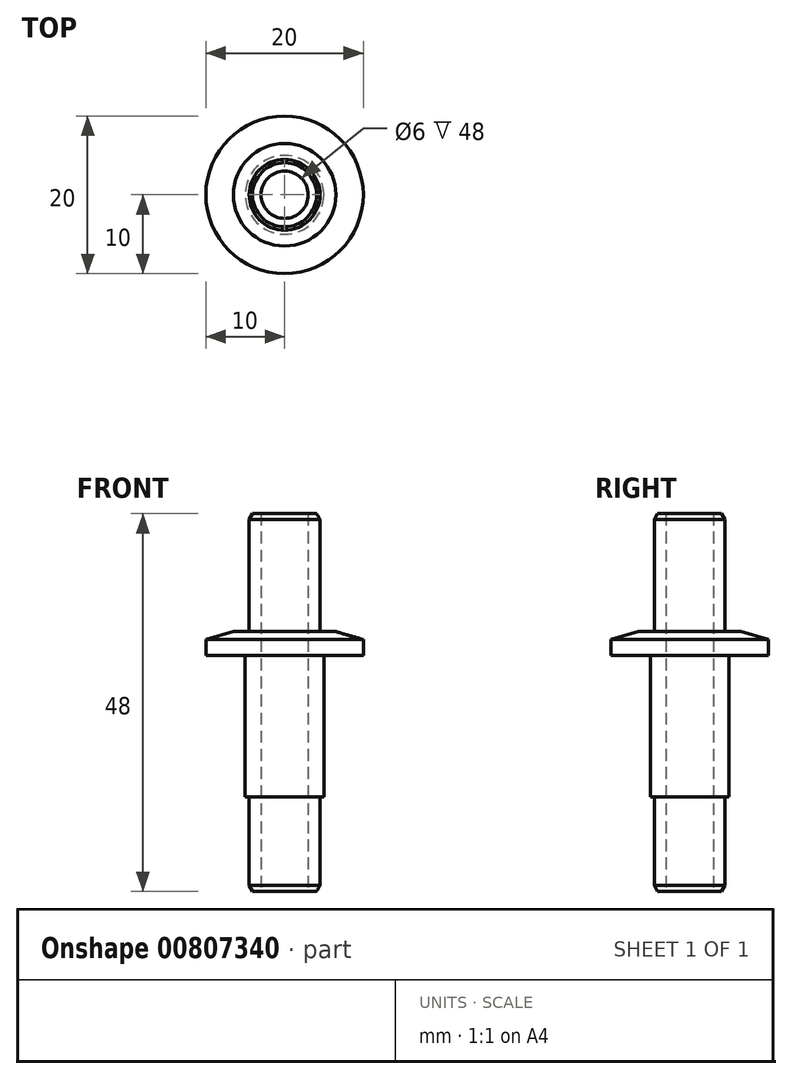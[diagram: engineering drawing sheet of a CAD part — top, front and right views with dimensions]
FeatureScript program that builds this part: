
annotation { "Feature Type Name" : "Feature", "Feature Type Description" : "" }
export const myFeature = defineFeature(function(context is Context, id is Id, definition is map)
    precondition{}
    {
        {
            var Q0;
            Q0=qCreatedBy(makeId("Top.planeOp"),FACE);
            var sketch = newSketch(context, id + "F0", { "sketchPlane" : qUnion([Q0])});
            skCircle(sketch, "E0", {"center": v(0, 0) * mm, "radius": 4.5 * mm});
            skSolve(sketch);
        }
        {
            var Q0;
            Q0 = qSketchRegion(id + "F0", true);
            extrude(context, id + "F1", {"entities" : qUnion([Q0]), "depth" : 12 * mm, "offsetDistance" : 25 * mm});
        }
        {
            var Q0;
            Q0=makeQuery(id+"F1.opExtrude","CAP_FACE",FACE,{"disambiguationData":[OSD([sQuery(id+"F0.wireOp",EDGE,"E0")])],"isStart":false});
            var sketch = newSketch(context, id + "F2", { "sketchPlane" : qUnion([Q0])});
            skCircle(sketch, "E1", {"center": v(0, 0) * mm, "radius": 5 * mm});
            skSolve(sketch);
        }
        {
            var Q0;
            Q0 = qSketchRegion(id + "F2", true);
            extrude(context, id + "F3", {"entities" : qUnion([Q0]), "operationType" : NewBodyOperationType.ADD, "depth" : 18 * mm, "offsetDistance" : 25 * mm});
        }
        {
            var Q0;
            Q0=makeQuery(id+"F3.opExtrude","CAP_FACE",FACE,{"disambiguationData":[OSD([sQuery(id+"F2.wireOp",EDGE,"E1")])],"isStart":false});
            var sketch = newSketch(context, id + "F4", { "sketchPlane" : qUnion([Q0])});
            skCircle(sketch, "E2", {"center": v(0, 0) * mm, "radius": 10 * mm});
            skSolve(sketch);
        }
        {
            var Q0;
            Q0 = qSketchRegion(id + "F4", true);
            extrude(context, id + "F5", {"entities" : qUnion([Q0]), "operationType" : NewBodyOperationType.ADD, "depth" : 3 * mm, "offsetDistance" : 25 * mm});
        }
        {
            var Q0;
            Q0=makeQuery(id+"F5.opExtrude","CAP_FACE",FACE,{"disambiguationData":[OSD([sQuery(id+"F4.wireOp",EDGE,"E2")])],"isStart":false});
            var sketch = newSketch(context, id + "F6", { "sketchPlane" : qUnion([Q0])});
            skCircle(sketch, "E3", {"center": v(0, 0) * mm, "radius": 4.5 * mm});
            skSolve(sketch);
        }
        {
            var Q0;
            Q0 = qSketchRegion(id + "F6", true);
            extrude(context, id + "F7", {"entities" : qUnion([Q0]), "operationType" : NewBodyOperationType.ADD, "depth" : 15 * mm, "offsetDistance" : 25 * mm});
        }
        {
            var Q0;
            Q0=makeQuery(id+"F1.opExtrude","CAP_FACE",FACE,{"disambiguationData":[OSD([sQuery(id+"F0.wireOp",EDGE,"E0")])],"isStart":true});
            var sketch = newSketch(context, id + "F8", { "sketchPlane" : qUnion([Q0])});
            skCircle(sketch, "E4", {"center": v(0, 0) * mm, "radius": 3 * mm});
            skSolve(sketch);
        }
        {
            var Q0;
            Q0 = qSketchRegion(id + "F8", true);
            extrude(context, id + "F9", {"entities" : qUnion([Q0]), "operationType" : NewBodyOperationType.REMOVE, "endBound" : BoundingType.THROUGH_ALL, "oppositeDirection" : true, "depth" : 25 * mm, "offsetDistance" : 25 * mm});
        }
        {
            var Q0;
            Q0=makeQuery(id+"F7.opExtrude","CAP_EDGE",EDGE,{"disambiguationData":[OSD([sQuery(id+"F6.wireOp",EDGE,"E3")])],"isStart":false});
            chamfer(context, id + "F10", {"entities" : qUnion([Q0]), "chamferType" : ChamferType.OFFSET_ANGLE, "width" : 0.75 * mm, "oppositeDirection" : true, "angle" : 30 * degree});
        }
        {
            var Q0;
            Q0=makeQuery(id+"F1.opExtrude","CAP_EDGE",EDGE,{"disambiguationData":[OSD([sQuery(id+"F0.wireOp",EDGE,"E0")])],"isStart":true});
            chamfer(context, id + "F11", {"entities" : qUnion([Q0]), "chamferType" : ChamferType.OFFSET_ANGLE, "width" : 0.75 * mm, "oppositeDirection" : false, "angle" : 30 * degree, "tangentPropagation" : true});
        }
        {
            var Q0;
            Q0=makeQuery(id+"F5.opExtrude","CAP_EDGE",EDGE,{"disambiguationData":[OSD([sQuery(id+"F4.wireOp",EDGE,"E2")])],"isStart":false});
            chamfer(context, id + "F12", {"entities" : qUnion([Q0]), "chamferType" : ChamferType.OFFSET_ANGLE, "width" : 1 * mm, "oppositeDirection" : true, "angle" : 74 * degree, "tangentPropagation" : true});
        }
    });
